# Revit family: PRD_AR_SoapDpnsrs_STRATOSSoapDispenser_STRX616,618,625
name_source: partatom
category: Specialty Equipment
revit_build: Autodesk Revit 2018 (Build: 20190510_1515(x64)
units: mm (PartAtom-declared; Revit-internal decimal feet)

## family parameters
Cut with Voids When Loaded = No
Host = Face
OmniClass Number = 23.40.20.21.34
OmniClass Title = Soap Holders, Dispensers
Part Type = Normal
Room Calculation Point = No
Round Connector Dimension = Use Diameter
Shared = No

## types (3) — shared parameters
AssetType = Fixed
Category = Pr_40_70_22_81, Soap dispensers
Color = Stainless steel
Default Elevation = 1050 mm
DurationUnit = year
Finish = Satin finished
Form = Wall mounted
IfcExportAs = IfcFurnitureType
IfcExportType = NOTDEFINED
IntegralAccessories = Incl. stainless steel screws and dowels
Lock = key-lock
MainColor = Stainless steel
Manufacturer = KWC Group AG
ManufacturerName = KWC Group AG
ManufacturerURL = www.kwc.com
Material = Stainless steel
MaterialsBody = Stainless steel
MaterialsFinishAndColour = Stainless steel, satin finished
NBSDescription = Soap dispensers
NBSReference = 45-35-72/358
Operation = Manual
ProductInformation = https://pim.kwc.com
SoapDispenserMaterial = PRD_AR_StainlessSteel_SatinFinished
Style = Soap dispenser
SurfaceTreatment = InoxPlus (anti fingerprint)
TypeOfMounting = Wall mounting
URL = www.kwc.com
Uniclass2015Code = Pr_40_70_22_81
Uniclass2015Title = Soap dispensers
Uniclass2015Version = Products v1.10
Version = 1
WarrantyDurationUnit = year

## per-type parameters (varying)
| type | BIMObjectName | Description | Features | FillingQuantity | GrossWeight | ModelNumber | Name | NetWeight | NominalDepth | NominalHeight | NominalLength | NominalWidth | NumberOfBatteries | Size | SparePartsAccessories | TypeOfBatteries | TypeOfConsumable | TypeOfOperation | TypeOfSoapContainer |
| STRX618 | PRD_AR_SpDpnsrs_EXOSSoapDispenser_STRX618 | Soap dispenser for wall mounting, stainless steel, surface satin finished, front with InoxPlus surface refinement for the reduction of finger marks and better cleaning characteristics (easy to clean), material thickness 1.5 mm, curved front cover, cylinder lock with KWC standard key, inspection window on front, suitable for liquid soaps and lotions, 0.8 liter soap tank, with plastic pull lever, incl. stainless steel screws and dowels. | stainless steel, 1.50 mm, satin finished, wall mounting, 100x304x134 mm (WxHxD) | 800 ml | 1.81 kg | 2000057379 | STRATOS Soap dispenser STRX618 | 1.70 kg | 134 mm | 304 mm  [stored 0.997375 ft] | 100 mm  [stored 0.328084 ft] | 100 mm  [stored 0.328084 ft] |  | 100x304x134 mm |  |  | Liquid soap | Manual operation | Integrated refillable bag |
| STRX616 | PRD_AR_SpDpnsrs_EXOSSoapDispenser_STRX616 | Foam soap dispenser for wall mounting, stainless steel, surface satin finished, front with InoxPlus surface refinement for the reduction of finger marks and better cleaning characteristics (easy to clean), material thickness 1.5 mm, curved front cover, cylinder lock with KWC standard key, inspection window on front, suitable for KWC foam soap, one bottle 650 ml foam soap included in first delivery, stainless steel pull lever, incl. stainless steel screws and dowels. | stainless steel, 1.50 mm, satin finished, wall mounting | 650 ml | 2.62 kg | 2000100001 | Foam soap dispenser STRX616 | 2.51 kg | 134 mm | 305 mm  [stored 1.00066 ft] | 112 mm  [stored 0.367454 ft] | 112 mm  [stored 0.367454 ft] |  | 134x305x112 mm |  |  | Foam soap | Manual operation | Single-use bag |
| STRX625 | PRD_AR_SpDpnsrs_EXOSSoapDispenser_STRX625 | Touch free soap dispenser for wall mounting, stainless steel, surface satin finished, front with InoxPlus surface refinement for the reduction of finger marks and better cleaning characteristics (easy to clean), material thickness 1.5 mm, curved front cover, cylinder lock with KWC standard key, inspection window on front, infrared sensor activity for non-touch operation, red light shows battery status, incl. 6 pcs. 1.5 V Alkaline AA batteries, suitable for liquid soaps and lotions, 0.8 liter soap tank, depending on soap between 0.6 and 1.1 ml is dispensed, mounting height >300 mm above wash basin or table top, incl. stainless steel screws and dowels. | stainless steel, 1.50 mm, satin finished, wall mounting | 800 ml | 2.47 kg | 2000057388 | Foam soap dispenser STRX625 | 2.17 kg | 126 mm  [stored 0.413386 ft] | 303 mm  [stored 0.994094 ft] | 120 mm  [stored 0.393701 ft] | 120 mm  [stored 0.393701 ft] | 6 | 126x303x120 mm | Dispending tube EACCS057 (2000103334) for the use with alcohol based disinfection soap. | AA Mignon battery 1.5 V | Liquid soap | Sensor operation | Integrated refillable tank |

note: column(s) folded — value = type name in every type: Model, ModelReference, Type

note: [stored X ft] marks values corroborated as IEEE doubles in the binary element streams (Revit-internal decimal feet)

## geometry (parser evidence)
native form markers: Sweep x10
no freeform markers — native parametric forms only
